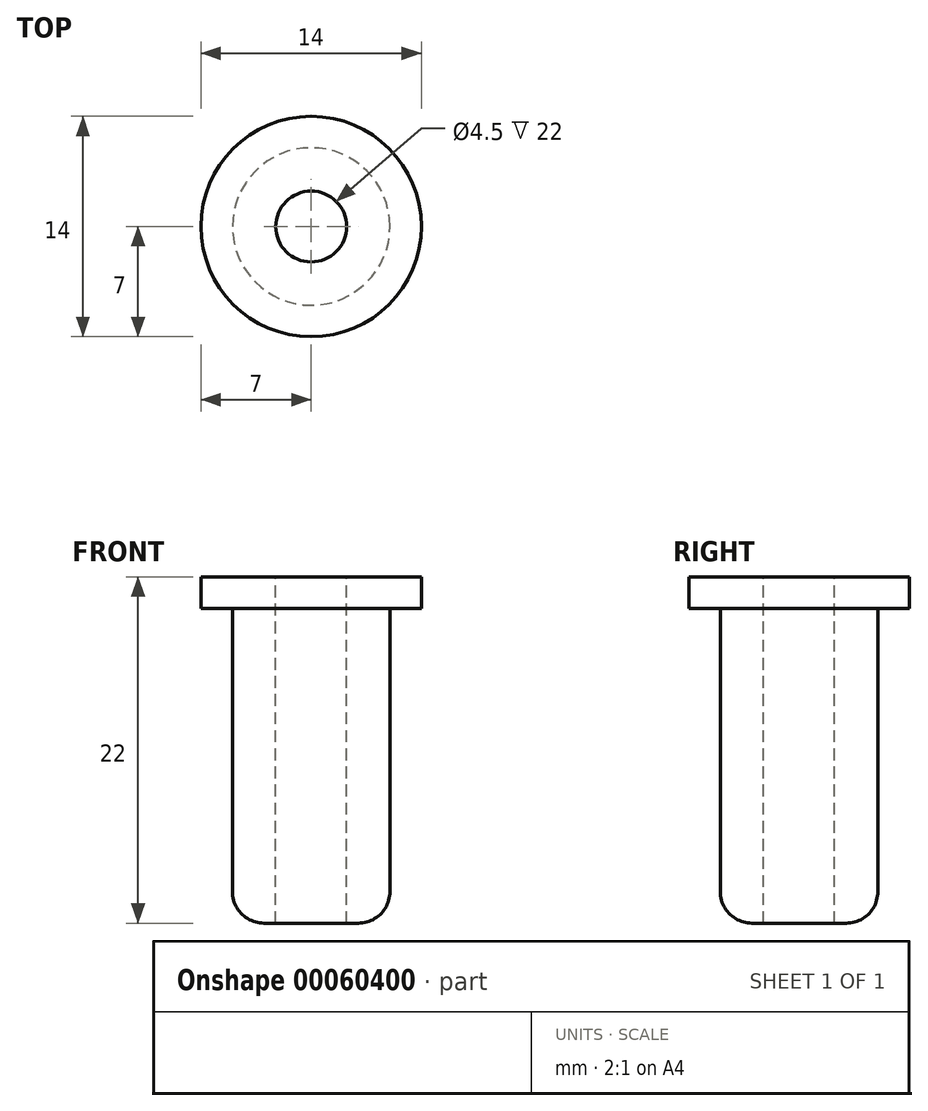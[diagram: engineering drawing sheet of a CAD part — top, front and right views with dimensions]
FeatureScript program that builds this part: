
annotation { "Feature Type Name" : "Feature", "Feature Type Description" : "" }
export const myFeature = defineFeature(function(context is Context, id is Id, definition is map)
    precondition{}
    {
        {
            var Q0;
            Q0=qCreatedBy(makeId("Top.planeOp"),FACE);
            var sketch = newSketch(context, id + "F0", { "sketchPlane" : qUnion([Q0])});
            skCircle(sketch, "E0", {"center": v(0, 0) * mm, "radius": 5 * mm});
            skCircle(sketch, "E1", {"center": v(0, 0) * mm, "radius": 2.25 * mm});
            skSolve(sketch);
        }
        {
            var Q0;
            Q0 = qSketchRegion(id + "F0", true);
            extrude(context, id + "F1", {"entities" : qUnion([Q0]), "oppositeDirection" : true, "depth" : 20 * mm});
        }
        {
            var Q0;
            Q0=makeQuery(id+"F1.opExtrude","CAP_EDGE",EDGE,{"disambiguationData":[OSD([sQuery(id+"F0.wireOp",EDGE,"E0")])],"isStart":false});
            fillet(context, id + "F2", {"entities" : qUnion([Q0]), "radius" : 2 * mm, "tangentPropagation" : true, "allowEdgeOverflow" : false});
        }
        {
            var Q0;
            Q0=makeQuery(id+"F1.opExtrude","CAP_FACE",FACE,{"disambiguationData":[OSD([sQuery(id+"F0.wireOp",EDGE,"E0"),sQuery(id+"F0.wireOp",EDGE,"E1")])],"isStart":true});
            var sketch = newSketch(context, id + "F3", { "sketchPlane" : qUnion([Q0])});
            skCircle(sketch, "E2", {"center": v(0, 0) * mm, "radius": 7 * mm});
            skCircle(sketch, "E3", {"center": v(0, 0) * mm, "radius": 2.25 * mm});
            skSolve(sketch);
        }
        {
            var Q0;
            Q0 = qSketchRegion(id + "F3", true);
            extrude(context, id + "F4", {"entities" : qUnion([Q0]), "operationType" : NewBodyOperationType.ADD, "depth" : 2 * mm});
        }
    });
